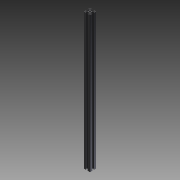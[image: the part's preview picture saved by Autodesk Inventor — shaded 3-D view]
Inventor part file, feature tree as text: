
AUTODESK INVENTOR PART (.ipt)
format: ipt  version: 2011 SP1 (Build 150282100, 282)  size: 185,344 bytes
history: native  units: mm
features: other x21, sketch x3, hole x2, extrude x1, pattern_linear x1
ambient origin geometry x8: Origin, YZ Plane, XZ Plane, XY Plane, X Axis, Y Axis, Z Axis, Center Point
bodies: Solid1 (feature_tree)
feature tree (28):
  extrude  "Extrusion1"  Depth=20.0mm
  hole  "Hole1"  [1 undecoded]
  hole  "Hole2"  [1 undecoded]
  pattern_linear  "Rectangular Pattern1"  [2 undecoded]
  other  "C1_XY"
  other  "C1_YZ"
  other  "C1_ZX"
  other  "C1_X"
  other  "C1_Y"
  other  "C1_Z"
  other  "C1_Center"
  other  "to_frame_cap1_XY"
  other  "to_frame_cap1_YZ"
  other  "to_frame_cap1_ZX"
  other  "to_frame_cap1_X"
  other  "to_frame_cap1_Y"
  other  "to_frame_cap1_Z"
  other  "to_frame_cap1_Center"
  other  "to_frame_cap2_XY"
  other  "to_frame_cap2_YZ"
  other  "to_frame_cap2_ZX"
  other  "to_frame_cap2_X"
  other  "to_frame_cap2_Y"
  other  "to_frame_cap2_Z"
  other  "to_frame_cap2_Center"
  sketch  "Sketch_1"  dims[d0=650.0mm d1=0.0mm]
  sketch  "Sketch2"  dims[d2=6.8mm d3=6.0mm d4=4.0mm d5=2.0mm d6=90.0deg d7=650.0mm d8=0.0mm]
  sketch  "Sketch3"  dims[d9=4.2mm d10=6.0mm d11=4.0mm d12=2.0mm d13=90.0deg d14=650.0mm d15=0.0mm d16=20.0mm d18=23.2mm d19=20.0mm d21=23.2mm d22=0.0mm d23=0.0mm d24=0.0mm]
note: 4 required parameter values undecoded (feature->parameter linkage not recoverable at this tier; creation-order binding heuristic only, values carry confidence <= 0.55)
